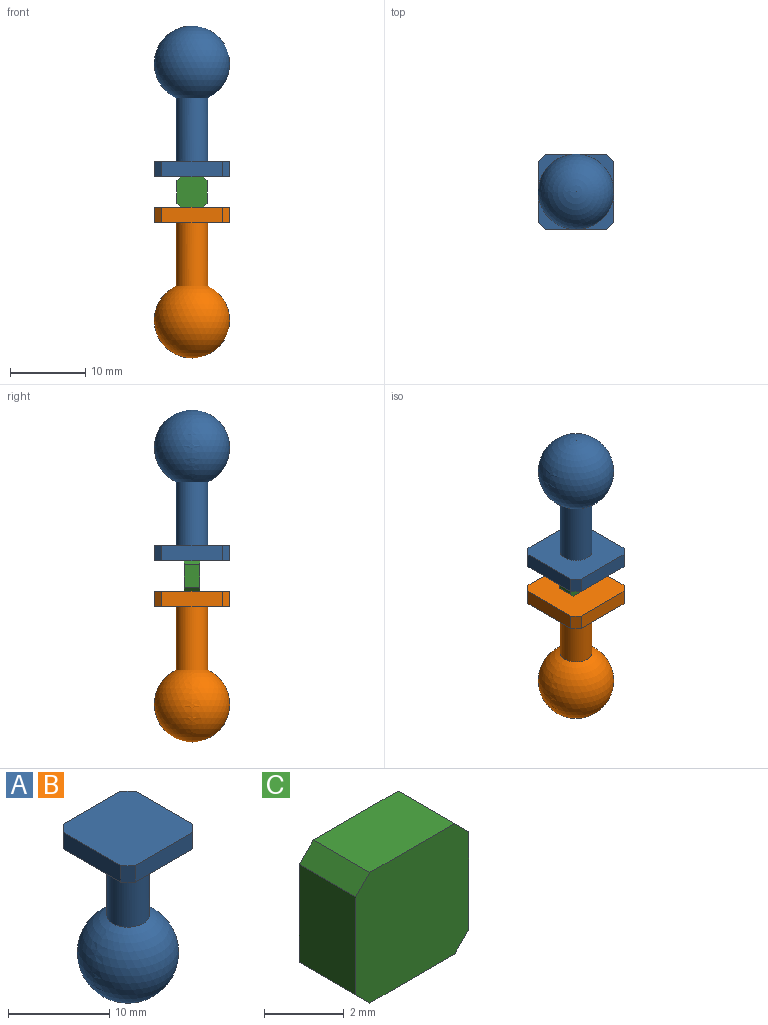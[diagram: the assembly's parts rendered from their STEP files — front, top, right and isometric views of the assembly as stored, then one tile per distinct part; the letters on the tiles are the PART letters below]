
ASSEMBLY  parts=3 mates=2
PART A: 12 faces, bbox 10x10x20 mm
  f0: cylinder r=2.1mm len=8.46mm, axis (0,0,-1), area 111.7mm2, adj f6,f7
  f1: plane 8x2mm, normal (1,0,0), area 16mm2, adj f5,f6,f9,f10
  f2: plane 8x2mm, normal (0,1,0), area 16mm2, adj f5,f6,f8,f9
  f3: plane 8x2mm, normal (-1,0,0), area 16mm2, adj f5,f6,f8,f11
  f4: plane 8x2mm, normal (0,-1,0), area 16mm2, adj f5,f6,f10,f11
  f5: plane 10x10mm, normal (0,0,1), area 98mm2, adj f1,f2,f3,f4,f8,f9,f10,f11
  f6: plane 10x10mm, normal (0,0,-1), area 84.1mm2, adj f0,f1,f2,f3,f4,f8,f9,f10
  f7: sphere r=5mm, area 299.6mm2, adj f0
  f8: plane 2x1mm, normal (-0.71,0.71,0), area 2.8mm2, adj f2,f3,f5,f6
  f9: plane 2x1mm, normal (0.71,0.71,0), area 2.8mm2, adj f1,f2,f5,f6
  f10: plane 2x1mm, normal (0.71,-0.71,0), area 2.8mm2, adj f1,f4,f5,f6
  f11: plane 2x1mm, normal (-0.71,-0.71,0), area 2.8mm2, adj f3,f4,f5,f6
PART B: same geometry as A
PART C: 10 faces, bbox 4x2x4 mm
  f0: plane 3x2mm, normal (-1,0,0), area 6mm2, adj f4,f5,f6,f7
  f1: plane 3x2mm, normal (0,0,-1), area 6mm2, adj f4,f5,f6,f9
  f2: plane 3x2mm, normal (1,0,0), area 6mm2, adj f4,f5,f8,f9
  f3: plane 3x2mm, normal (0,0,1), area 6mm2, adj f4,f5,f7,f8
  f4: plane 4x4mm, normal (0,-1,0), area 15.5mm2, adj f0,f1,f2,f3,f6,f7,f8,f9
  f5: plane 4x4mm, normal (0,1,0), area 15.5mm2, adj f0,f1,f2,f3,f6,f7,f8,f9
  f6: plane 2x0.5mm, normal (-0.71,0,-0.71), area 1.4mm2, adj f0,f1,f4,f5
  f7: plane 2x0.5mm, normal (-0.71,0,0.71), area 1.4mm2, adj f0,f3,f4,f5
  f8: plane 2x0.5mm, normal (0.71,0,0.71), area 1.4mm2, adj f2,f3,f4,f5
  f9: plane 2x0.5mm, normal (0.71,0,-0.71), area 1.4mm2, adj f1,f2,f4,f5
PLACE A rot(axis=(1,0,0),180deg) t=(3.42,2.39,25.62)mm
PLACE B t=(3.42,2.39,-0.38)mm
PLACE C rot(axis=(1,0,0),180deg) t=(-21.44,1.39,7.14)mm
MATE fastened A.f0 <-> C.f1  axis (0,0,-1) through (3.42,2.39,14.62)mm
MATE fastened C.f3 <-> B.f0  axis (0,0,-1) through (3.42,2.39,10.62)mm
